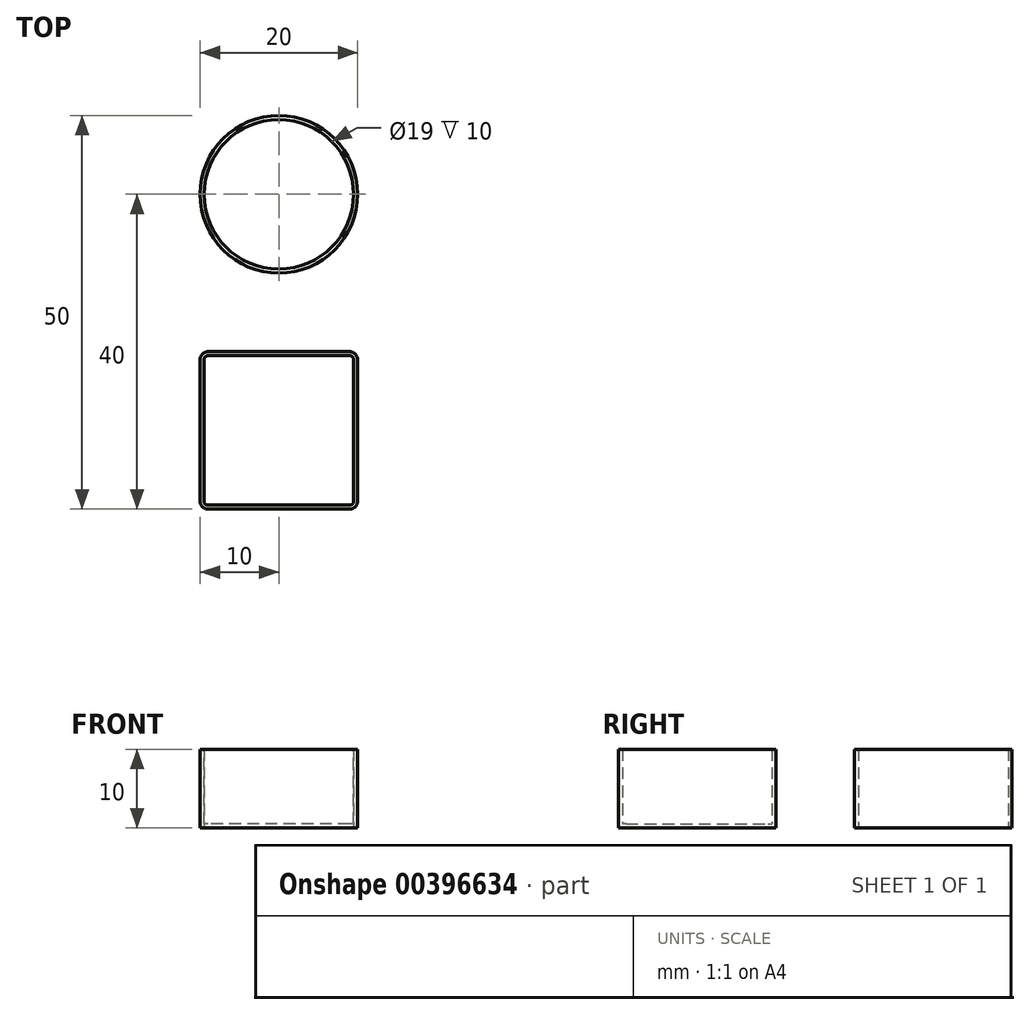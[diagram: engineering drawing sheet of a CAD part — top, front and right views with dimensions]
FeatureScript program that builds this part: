
annotation { "Feature Type Name" : "Feature", "Feature Type Description" : "" }
export const myFeature = defineFeature(function(context is Context, id is Id, definition is map)
    precondition{}
    {
        {
            var Q0;
            Q0=qCreatedBy(makeId("Top.planeOp"),FACE);
            var sketch = newSketch(context, id + "F0", { "sketchPlane" : qUnion([Q0])});
            skCircle(sketch, "E0", {"center": v(0, 0) * mm, "radius": 10 * mm});
            skCircle(sketch, "E1", {"center": v(0, 0) * mm, "radius": 9.5 * mm});
            skSolve(sketch);
        }
        {
            var Q0;
            Q0 = qSketchRegion(id + "F0", true);
            extrude(context, id + "F1", {"entities" : qUnion([Q0]), "depth" : 10 * mm});
        }
        {
            var Q0;
            Q0=qCreatedBy(makeId("Top.planeOp"),FACE);
            var sketch = newSketch(context, id + "F2", { "sketchPlane" : qUnion([Q0])});
            skLineSegment(sketch, "E2.bottom", {"start": v(9, -40) * mm, "end": v(-9, -40) * mm});
            skLineSegment(sketch, "E2.top", {"start": v(9, -20) * mm, "end": v(-9, -20) * mm});
            skLineSegment(sketch, "E2.left", {"start": v(10, -39) * mm, "end": v(10, -21) * mm});
            skLineSegment(sketch, "E2.right", {"start": v(-10, -39) * mm, "end": v(-10, -21) * mm});
            skPoint(sketch, "E2.middle", {"position": v(0, -30) * mm});
            skPoint(sketch, "E3.visualSharp", {"position": v(-10, -20) * mm});
            skArc(sketch, "E3.filletArc", {"start": v(-9, -20) * mm, "mid": v(-9.7, -20.3) * mm, "end": v(-10, -21) * mm});
            skPoint(sketch, "E4.visualSharp", {"position": v(10, -20) * mm});
            skArc(sketch, "E4.filletArc", {"start": v(10, -21) * mm, "mid": v(9.7, -20.3) * mm, "end": v(9, -20) * mm});
            skPoint(sketch, "E5.visualSharp", {"position": v(10, -40) * mm});
            skArc(sketch, "E5.filletArc", {"start": v(9, -40) * mm, "mid": v(9.7, -39.7) * mm, "end": v(10, -39) * mm});
            skPoint(sketch, "E6.visualSharp", {"position": v(-10, -40) * mm});
            skArc(sketch, "E6.filletArc", {"start": v(-10, -39) * mm, "mid": v(-9.7, -39.7) * mm, "end": v(-9, -40) * mm});
            skSolve(sketch);
        }
        {
            var Q0;
            Q0 = qSketchRegion(id + "F2", true);
            extrude(context, id + "F3", {"entities" : qUnion([Q0]), "depth" : 10 * mm});
        }
        {
            var Q0;
            Q0=makeQuery(id+"F3.opExtrude","CAP_FACE",FACE,{"disambiguationData":[OSD([sQuery(id+"F2.wireOp",EDGE,"E2.bottom"),sQuery(id+"F2.wireOp",EDGE,"E2.top"),sQuery(id+"F2.wireOp",EDGE,"E2.left"),sQuery(id+"F2.wireOp",EDGE,"E2.right"),sQuery(id+"F2.wireOp",EDGE,"E3.filletArc"),sQuery(id+"F2.wireOp",EDGE,"E4.filletArc"),sQuery(id+"F2.wireOp",EDGE,"E5.filletArc"),sQuery(id+"F2.wireOp",EDGE,"E6.filletArc")])],"isStart":false});
            var Q1;
            Q1=makeQuery(id+"F3.opExtrude","SWEPT_BODY",BODY,{"disambiguationData":[OSD([sQuery(id+"F2.wireOp",EDGE,"E2.bottom"),sQuery(id+"F2.wireOp",EDGE,"E2.top"),sQuery(id+"F2.wireOp",EDGE,"E2.left"),sQuery(id+"F2.wireOp",EDGE,"E2.right"),sQuery(id+"F2.wireOp",EDGE,"E3.filletArc"),sQuery(id+"F2.wireOp",EDGE,"E4.filletArc"),sQuery(id+"F2.wireOp",EDGE,"E5.filletArc"),sQuery(id+"F2.wireOp",EDGE,"E6.filletArc")])]});
            shell(context, id + "F4", {"entities" : qUnion([Q0]), "parts" : qUnion([Q1]), "thickness" : 0.5 * mm});
        }
    });
